# Revit family: Sanitary_Showers_hansgrohe_28788XXX-Jocolino-Children-hand-shower-c_9
name_source: partatom
category: Plumbing Fixtures
revit_build: Autodesk Revit 2018 (Build: 20170223_1515(x64)
units: mm (PartAtom-declared; Revit-internal decimal feet)

## family parameters
Always vertical = No
Cut with Voids When Loaded = No
OmniClass Number = 23.45.05.14.17
OmniClass Title = Showers
Part Type = Normal
Room Calculation Point = No
Round Connector Dimension = Use Diameter
Shared = No
Work Plane-Based = Yes

## types (1)
- 28788XXX Jocolino Children hand shower crocodile 2jet
    Always visible = Yes
    BIMobject category = Showers
    Default Elevation = 1219.2 mm  [stored 4 ft]
    Description = Jocolino Children hand shower crocodile 2jet
    Design country = Germany
    EAN code = 4059625361375
    Edition number = 1
    IFC Classification = Sanitary Terminal
    Manufacturer = hansgrohe
    Manufacturer country = Germany
    Manufacturer name = hansgrohe
    Masterformat 2014 Code = 22 41 23
    Masterformat 2014 Description = Residential Showers
    Material 1 = Hansgrohe - Plastic - Gray
    Material 2 = Hansgrohe - Plastic - Green Plastic
    Material 3 = Hansgrohe - Plastic - Dark Green
    Material 4 = Hansgrohe - Plastic - Mat White
    Material 5 = Hansgrohe - Metal - 000 Chrome
    Material 6 = Hansgrohe - Plastic - White
    Material 7 = Hansgrohe - Plastic - Transparent_White
    Material 8 = Hansgrohe - Plastic - Black
    Material main = Plastic
    Model = 28788XXX
    NBS Reference Code = 35-06-81
    NBS Reference Description = Shower Heads
    OmniClass Code = 23-31 17 00
    OmniClass Description = Showers
    Product Guid = 3bfcdedb-be3c-4a3e-9257-32416a4dbb22
    Product SKU = 28788XXX
    Product data url = https://bimobject.com
    Product family = Jocolino
    Product group = Hand showers
    Product name = 28788XXX Jocolino Children hand shower crocodile 2jet
    QR code = https://bimobject.com
    UNSPSC Code = 30181503
    URL = https://www.hansgrohe.com
    Uniclass 2015 Code = Pr_40_20_87_76
    Uniclass 2015 Name = Shower heads
    Uniformat II Code = D2010
    Uniformat II Description = Plumbing Fixtures
    Water Inlet = 12.7 mm  [stored 0.0416667 ft]
    Weight Net (Kg) = 144

note: [stored X ft] marks values corroborated as IEEE doubles in the binary element streams (Revit-internal decimal feet)

## geometry (parser evidence)
native form markers: Sweep x4
no freeform markers — native parametric forms only
